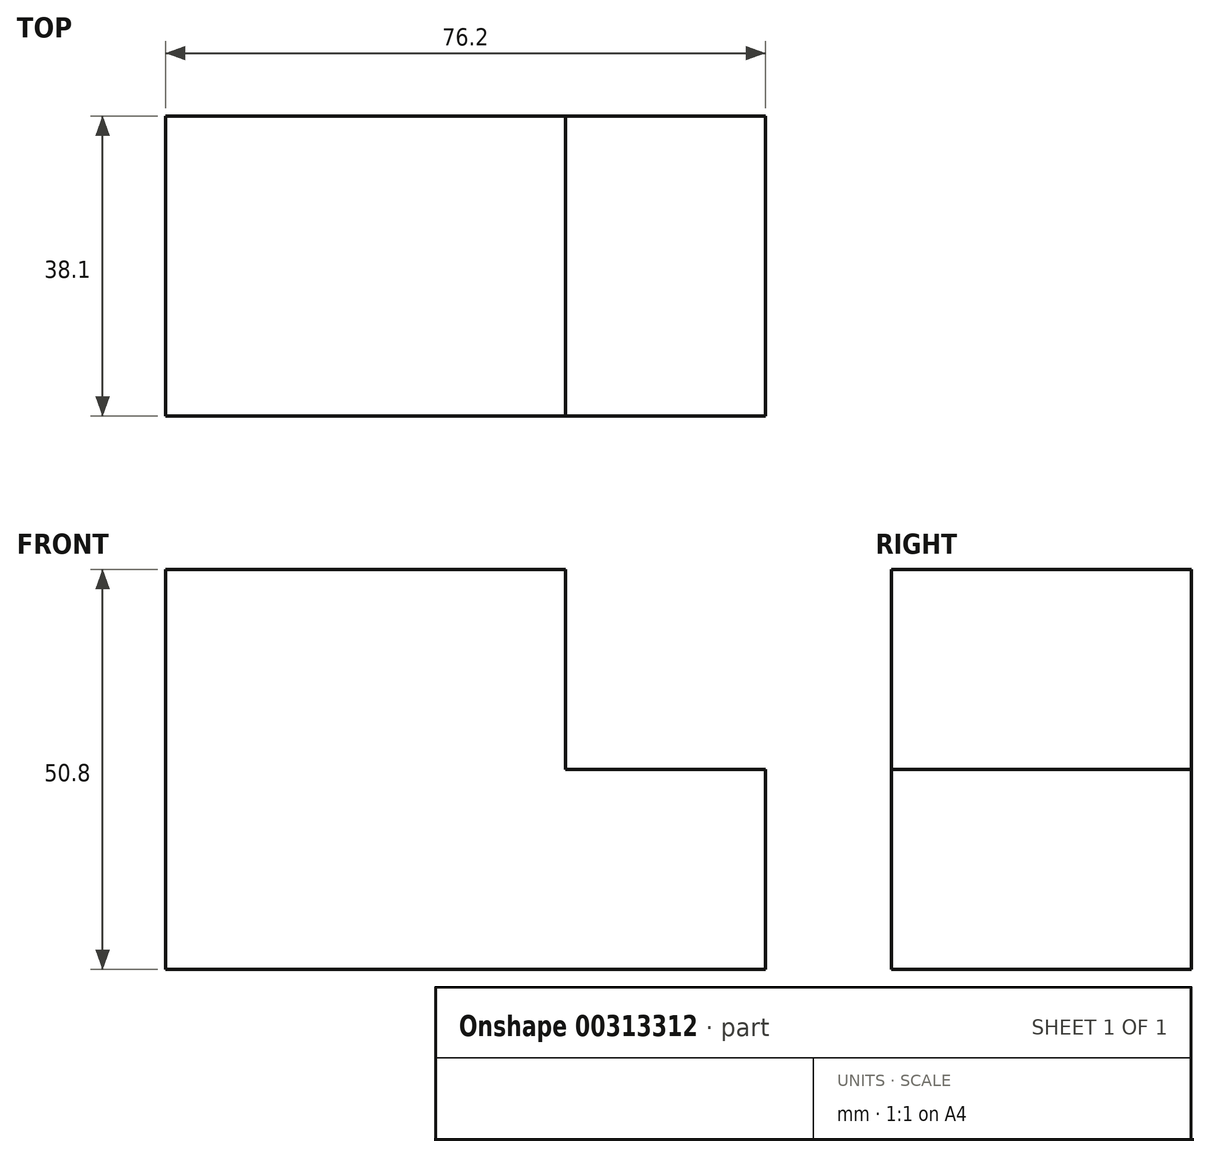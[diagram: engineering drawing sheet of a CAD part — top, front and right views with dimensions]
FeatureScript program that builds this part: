
annotation { "Feature Type Name" : "Feature", "Feature Type Description" : "" }
export const myFeature = defineFeature(function(context is Context, id is Id, definition is map)
    precondition{}
    {
        {
            var Q0;
            Q0=qCreatedBy(makeId("Front.planeOp"),FACE);
            var sketch = newSketch(context, id + "F0", { "sketchPlane" : qUnion([Q0])});
            skLineSegment(sketch, "E0", {"start": v(-43.32, -51.55) * mm, "end": v(32.88, -51.55) * mm});
            skLineSegment(sketch, "E1", {"start": v(32.88, -51.55) * mm, "end": v(32.88, -26.15) * mm});
            skLineSegment(sketch, "E2", {"start": v(32.88, -26.15) * mm, "end": v(7.48, -26.15) * mm});
            skLineSegment(sketch, "E3", {"start": v(7.48, -26.15) * mm, "end": v(7.48, -0.75) * mm});
            skLineSegment(sketch, "E4", {"start": v(7.48, -0.75) * mm, "end": v(-43.32, -0.75) * mm});
            skLineSegment(sketch, "E5", {"start": v(-43.32, -0.75) * mm, "end": v(-43.32, -51.55) * mm});
            skSolve(sketch);
        }
        {
            var Q0;
            Q0=makeQuery(id+"F0.imprint","IMPRINT",FACE,{"disambiguationData":[TD([[makeQuery(id+"F0.imprint","IMPRINT",EDGE,{"derivedFrom":sQuery(id+"F0.wireOp",EDGE,"E0")}),1.0]])]});
            extrude(context, id + "F1", {"entities" : qUnion([Q0]), "depth" : 38.1 * mm});
        }
    });
